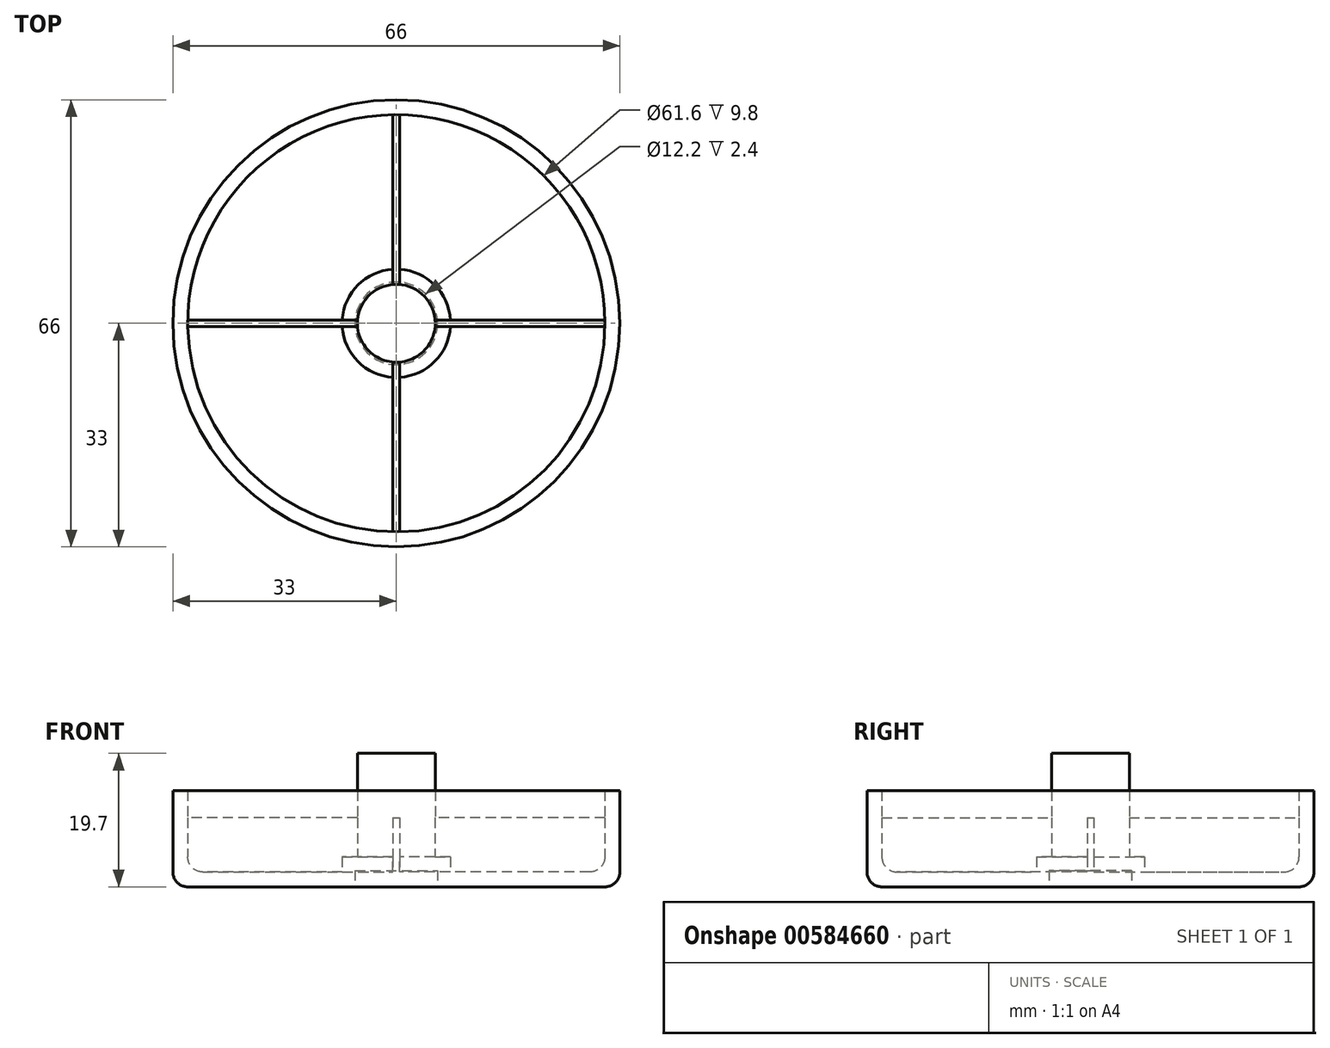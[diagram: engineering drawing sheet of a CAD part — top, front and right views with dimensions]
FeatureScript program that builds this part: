
annotation { "Feature Type Name" : "Feature", "Feature Type Description" : "" }
export const myFeature = defineFeature(function(context is Context, id is Id, definition is map)
    precondition{}
    {
        {
            var Q0;
            Q0=qCreatedBy(makeId("Top.planeOp"),FACE);
            var sketch = newSketch(context, id + "F0", { "sketchPlane" : qUnion([Q0])});
            skCircle(sketch, "E0", {"center": v(0, 0) * mm, "radius": 33 * mm});
            skSolve(sketch);
        }
        {
            var Q0;
            Q0=makeQuery(id+"F0.imprint","IMPRINT",FACE,{"disambiguationData":[TD([[makeQuery(id+"F0.imprint","IMPRINT",EDGE,{"derivedFrom":sQuery(id+"F0.wireOp",EDGE,"E0")}),1.0]])]});
            extrude(context, id + "F1", {"entities" : qUnion([Q0]), "depth" : 2.2 * mm, "offsetDistance" : 25 * mm});
        }
        {
            var Q0;
            Q0=makeQuery(id+"F1.opExtrude","CAP_FACE",FACE,{"disambiguationData":[OSD([sQuery(id+"F0.wireOp",EDGE,"E0")])],"isStart":false});
            var sketch = newSketch(context, id + "F2", { "sketchPlane" : qUnion([Q0])});
            skCircle(sketch, "E1", {"center": v(0, 0) * mm, "radius": 33 * mm});
            skCircle(sketch, "E2", {"center": v(0, 0) * mm, "radius": 30.8 * mm});
            skSolve(sketch);
        }
        {
            var Q0;
            Q0 = qSketchRegion(id + "F2", true);
            extrude(context, id + "F3", {"entities" : qUnion([Q0]), "operationType" : NewBodyOperationType.ADD, "depth" : 12 * mm, "offsetDistance" : 25 * mm});
        }
        {
            var Q0;
            Q0=makeQuery(id+"F1.opExtrude","CAP_EDGE",EDGE,{"disambiguationData":[OSD([sQuery(id+"F0.wireOp",EDGE,"E0")])],"isStart":true});
            fillet(context, id + "F4", {"entities" : qUnion([Q0]), "radius" : 2.2 * mm, "tangentPropagation" : true, "allowEdgeOverflow" : false});
        }
        {
            var Q0;
            Q0=makeQuery(id+"F1.opExtrude","CAP_FACE",FACE,{"disambiguationData":[OSD([sQuery(id+"F0.wireOp",EDGE,"E0")])],"isStart":false});
            fillet(context, id + "F5", {"entities" : qUnion([Q0]), "radius" : 2.2 * mm, "tangentPropagation" : true, "allowEdgeOverflow" : false});
        }
        {
            var Q0;
            Q0=makeQuery(id+"F1.opExtrude","CAP_FACE",FACE,{"disambiguationData":[OSD([sQuery(id+"F0.wireOp",EDGE,"E0")])],"isStart":false});
            var sketch = newSketch(context, id + "F6", { "sketchPlane" : qUnion([Q0])});
            skCircle(sketch, "E3", {"center": v(0, 0) * mm, "radius": 8 * mm});
            skSolve(sketch);
        }
        {
            var Q0;
            Q0=makeQuery(id+"F6.imprint","IMPRINT",FACE,{"disambiguationData":[TD([[makeQuery(id+"F6.imprint","IMPRINT",EDGE,{"derivedFrom":sQuery(id+"F6.wireOp",EDGE,"E3")}),1.0]])]});
            extrude(context, id + "F7", {"entities" : qUnion([Q0]), "operationType" : NewBodyOperationType.ADD, "depth" : 2.2 * mm, "offsetDistance" : 25 * mm});
        }
        {
            var Q0;
            Q0=makeQuery(id+"F7.opExtrude","CAP_FACE",FACE,{"disambiguationData":[OSD([sQuery(id+"F6.wireOp",EDGE,"E3")])],"isStart":false});
            var sketch = newSketch(context, id + "F8", { "sketchPlane" : qUnion([Q0])});
            skCircle(sketch, "E4", {"center": v(0, 0) * mm, "radius": 5.75 * mm});
            skSolve(sketch);
        }
        {
            var Q0;
            Q0=makeQuery(id+"F8.imprint","IMPRINT",FACE,{"disambiguationData":[TD([[makeQuery(id+"F8.imprint","IMPRINT",EDGE,{"derivedFrom":sQuery(id+"F8.wireOp",EDGE,"E4")}),1.0]])]});
            extrude(context, id + "F9", {"entities" : qUnion([Q0]), "operationType" : NewBodyOperationType.ADD, "depth" : 15.3 * mm, "offsetDistance" : 25 * mm});
        }
        {
            var Q0;
            Q0=makeQuery(id+"Fr3TDggzBYmpdjE_1.boolean.opBoolean","SPLIT",FACE,{"disambiguationData":[TD([makeQuery(id+"Fr3TDggzBYmpdjE_1.opExtrude","SWEPT_FACE",FACE,{"disambiguationData":[OSD([sQuery(id+"F5FMOYiURHPtZCy_1.wireOp",EDGE,"3719a7f2-0e31-46e7-8cbf-c82bd3d27626.bottom")])]})])],"derivedFrom":makeQuery(id+"F1.opExtrude","CAP_FACE",FACE,{"disambiguationData":[OSD([sQuery(id+"F0.wireOp",EDGE,"E0")])],"isStart":false})});
            var sketch = newSketch(context, id + "F10", { "sketchPlane" : qUnion([Q0])});
            skLineSegment(sketch, "E5.bottom", {"start": v(0.5, -31.5) * mm, "end": v(-0.5, -31.5) * mm});
            skLineSegment(sketch, "E5.top", {"start": v(0.5, 31.5) * mm, "end": v(-0.5, 31.5) * mm});
            skLineSegment(sketch, "E5.left", {"start": v(0.5, -31.5) * mm, "end": v(0.5, 31.5) * mm});
            skLineSegment(sketch, "E5.right", {"start": v(-0.5, -31.5) * mm, "end": v(-0.5, 31.5) * mm});
            skPoint(sketch, "E5.middle", {"position": v(0, 0) * mm});
            skSolve(sketch);
        }
        {
            var Q0;
            Q0 = qSketchRegion(id + "F10", true);
            extrude(context, id + "F11", {"entities" : qUnion([Q0]), "operationType" : NewBodyOperationType.ADD, "depth" : 8 * mm, "offsetDistance" : 25 * mm});
        }
        {
            var Q0;
            Q0=makeQuery(id+"F11.boolean.opBoolean","SPLIT",FACE,{"disambiguationData":[TD([makeQuery(id+"F11.opExtrude","SWEPT_FACE",FACE,{"disambiguationData":[OSD([sQuery(id+"F10.wireOp",EDGE,"E5.right")])]})])],"derivedFrom":makeQuery(id+"F1.opExtrude","CAP_FACE",FACE,{"disambiguationData":[OSD([sQuery(id+"F0.wireOp",EDGE,"E0")])],"isStart":false})});
            var sketch = newSketch(context, id + "F12", { "sketchPlane" : qUnion([Q0])});
            skLineSegment(sketch, "E6.bottom", {"start": v(31.5, 0.5) * mm, "end": v(-31.5, 0.5) * mm});
            skLineSegment(sketch, "E6.top", {"start": v(31.5, -0.5) * mm, "end": v(-31.5, -0.5) * mm});
            skLineSegment(sketch, "E6.left", {"start": v(31.5, 0.5) * mm, "end": v(31.5, -0.5) * mm});
            skLineSegment(sketch, "E6.right", {"start": v(-31.5, 0.5) * mm, "end": v(-31.5, -0.5) * mm});
            skPoint(sketch, "E6.middle", {"position": v(0, 0) * mm});
            skSolve(sketch);
        }
        {
            var Q0;
            Q0 = qSketchRegion(id + "F12", true);
            extrude(context, id + "F13", {"entities" : qUnion([Q0]), "operationType" : NewBodyOperationType.ADD, "depth" : 8 * mm, "offsetDistance" : 25 * mm});
        }
        {
            var Q0;
            Q0=makeQuery(id+"F1.opExtrude","CAP_FACE",FACE,{"disambiguationData":[OSD([sQuery(id+"F0.wireOp",EDGE,"E0")])],"isStart":true});
            var sketch = newSketch(context, id + "F14", { "sketchPlane" : qUnion([Q0])});
            skPoint(sketch, "E7", {"position": v(0, 0) * mm});
            skSolve(sketch);
        }
        {
            var Q0;
            Q0=sQuery(id+"F14.wireOp",VERTEX,"E7");
            var Q1;
            Q1=makeQuery(id+"F1.opExtrude","SWEPT_BODY",BODY,{"disambiguationData":[OSD([sQuery(id+"F0.wireOp",EDGE,"E0")])]});
            hole(context, id + "F15", {"style" : HoleStyle.C_BORE, "endStyle" : HoleEndStyle.BLIND, "holeDiameter" : 0.01 * mm, "cBoreDiameter" : 12.2 * mm, "cBoreDepth" : 2.4 * mm, "majorDiameter" : 5 * mm, "holeDepth" : 2.4 * mm, "isTappedThrough" : true, "tappedDepth" : 12 * mm, "tapClearance" : 3, "locations" : qUnion([Q0]), "scope" : qUnion([Q1])});
        }
    });
